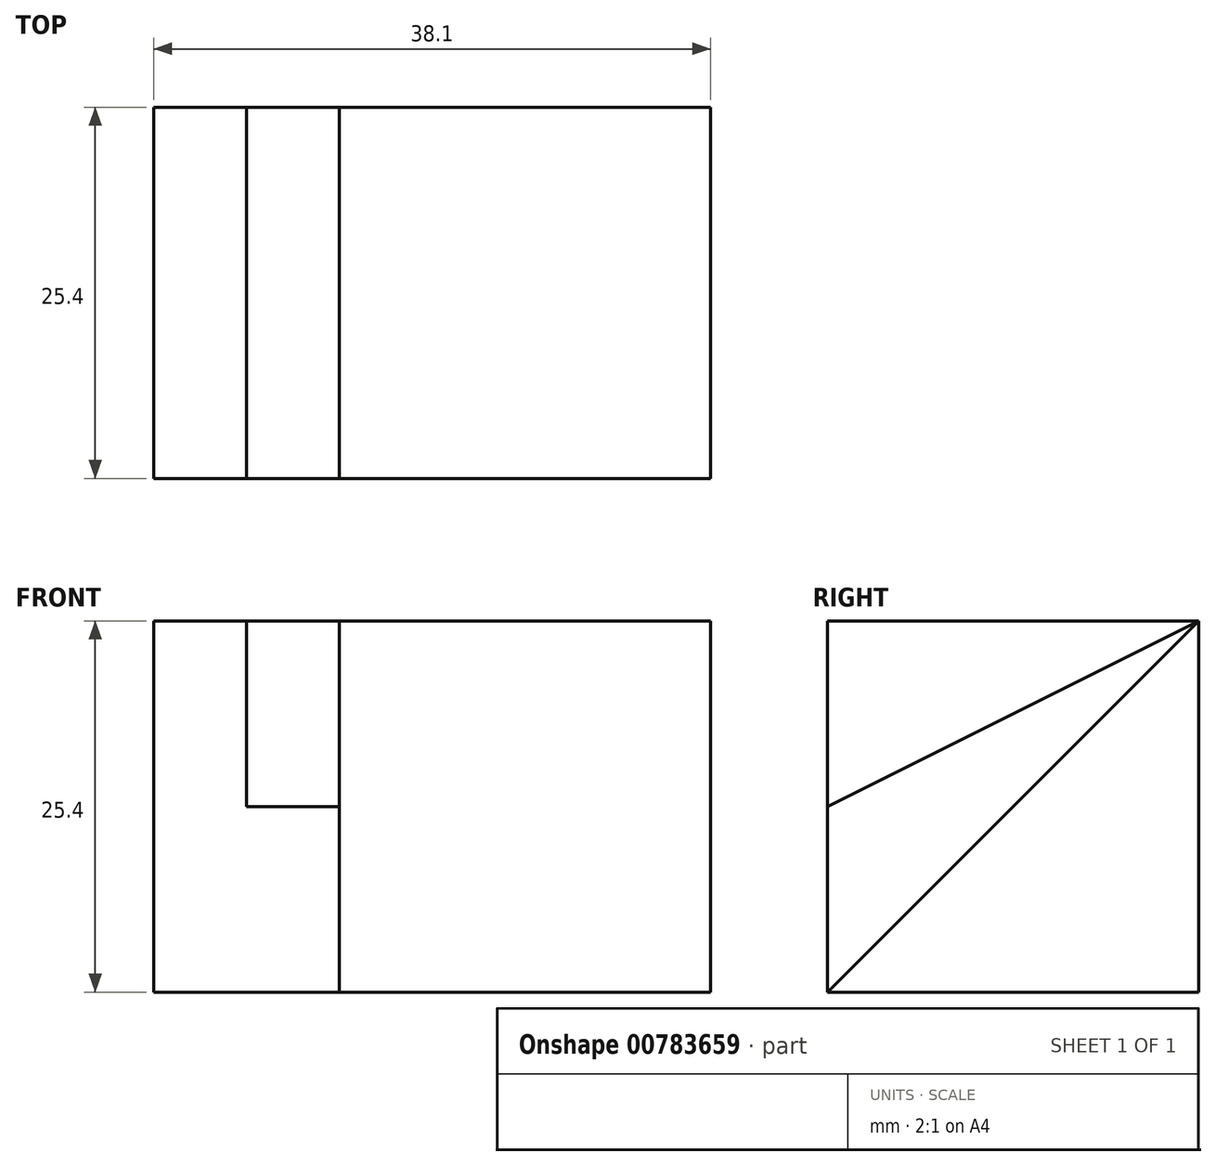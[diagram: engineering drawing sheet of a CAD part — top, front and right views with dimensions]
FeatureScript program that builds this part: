
annotation { "Feature Type Name" : "Feature", "Feature Type Description" : "" }
export const myFeature = defineFeature(function(context is Context, id is Id, definition is map)
    precondition{}
    {
        {
            var Q0;
            Q0=qCreatedBy(makeId("Right.planeOp"),FACE);
            var sketch = newSketch(context, id + "F0", { "sketchPlane" : qUnion([Q0])});
            skLineSegment(sketch, "E0", {"start": v(0, 0) * mm, "end": v(25.4, 0) * mm});
            skLineSegment(sketch, "E1", {"start": v(25.4, 0) * mm, "end": v(25.4, 25.4) * mm});
            skLineSegment(sketch, "E2", {"start": v(25.4, 25.4) * mm, "end": v(0, 25.4) * mm});
            skLineSegment(sketch, "E3", {"start": v(0, 25.4) * mm, "end": v(0, 0) * mm});
            skLineSegment(sketch, "E4", {"start": v(0, 25.4) * mm, "end": v(0, 12.7) * mm});
            skLineSegment(sketch, "E5", {"start": v(0, 12.7) * mm, "end": v(25.4, 25.4) * mm});
            skLineSegment(sketch, "E6", {"start": v(0, 0) * mm, "end": v(25.4, 25.4) * mm});
            skSolve(sketch);
        }
        {
            var Q0;
            Q0 = qSketchRegion(id + "F0", true);
            extrude(context, id + "F1", {"entities" : qUnion([Q0]), "depth" : 38.1 * mm, "offsetDistance" : 25.4 * mm});
        }
        {
            var Q0;
            Q0=makeQuery(id+"F1.opExtrude","CAP_FACE",FACE,{"disambiguationData":[OSD([sQuery(id+"F0.wireOp",EDGE,"E0"),sQuery(id+"F0.wireOp",EDGE,"E1"),sQuery(id+"F0.wireOp",EDGE,"E2"),sQuery(id+"F0.wireOp",EDGE,"E3"),sQuery(id+"F0.wireOp",EDGE,"E4")])],"isStart":false});
            var sketch = newSketch(context, id + "F2", { "sketchPlane" : qUnion([Q0])});
            skLineSegment(sketch, "E7", {"start": v(0, 25.4) * mm, "end": v(0, 12.7) * mm});
            skLineSegment(sketch, "E8", {"start": v(0, 12.7) * mm, "end": v(25.4, 25.4) * mm});
            skLineSegment(sketch, "E9", {"start": v(0, 0) * mm, "end": v(25.4, 25.4) * mm});
            skSolve(sketch);
        }
        {
            var Q0;
            Q0=makeQuery(id+"F2.imprint","IMPRINT",FACE,{"disambiguationData":[TD([[makeQuery(id+"F2.imprint","IMPRINT",EDGE,{"derivedFrom":sQuery(id+"F2.wireOp",EDGE,"E7")}),1.0]])]});
            extrude(context, id + "F3", {"entities" : qUnion([Q0]), "operationType" : NewBodyOperationType.REMOVE, "oppositeDirection" : true, "depth" : 31.75 * mm, "offsetDistance" : 25.4 * mm});
        }
        {
            var Q0;
            Q0=makeQuery(id+"F1.opExtrude","CAP_FACE",FACE,{"disambiguationData":[OSD([sQuery(id+"F0.wireOp",EDGE,"E0"),sQuery(id+"F0.wireOp",EDGE,"E1"),sQuery(id+"F0.wireOp",EDGE,"E2"),sQuery(id+"F0.wireOp",EDGE,"E3"),sQuery(id+"F0.wireOp",EDGE,"E4")])],"isStart":false});
            var sketch = newSketch(context, id + "F4", { "sketchPlane" : qUnion([Q0])});
            skLineSegment(sketch, "E10", {"start": v(0, 0) * mm, "end": v(25.4, 25.4) * mm});
            skSolve(sketch);
        }
        {
            var Q0;
            Q0=makeQuery(id+"F4.imprint","IMPRINT",FACE,{"disambiguationData":[TD([[makeQuery(id+"F4.imprint","IMPRINT",EDGE,{"derivedFrom":sQuery(id+"F4.wireOp",EDGE,"E10")}),1.0]])]});
            extrude(context, id + "F5", {"entities" : qUnion([Q0]), "operationType" : NewBodyOperationType.REMOVE, "oppositeDirection" : true, "depth" : 25.4 * mm, "offsetDistance" : 25.4 * mm});
        }
    });
